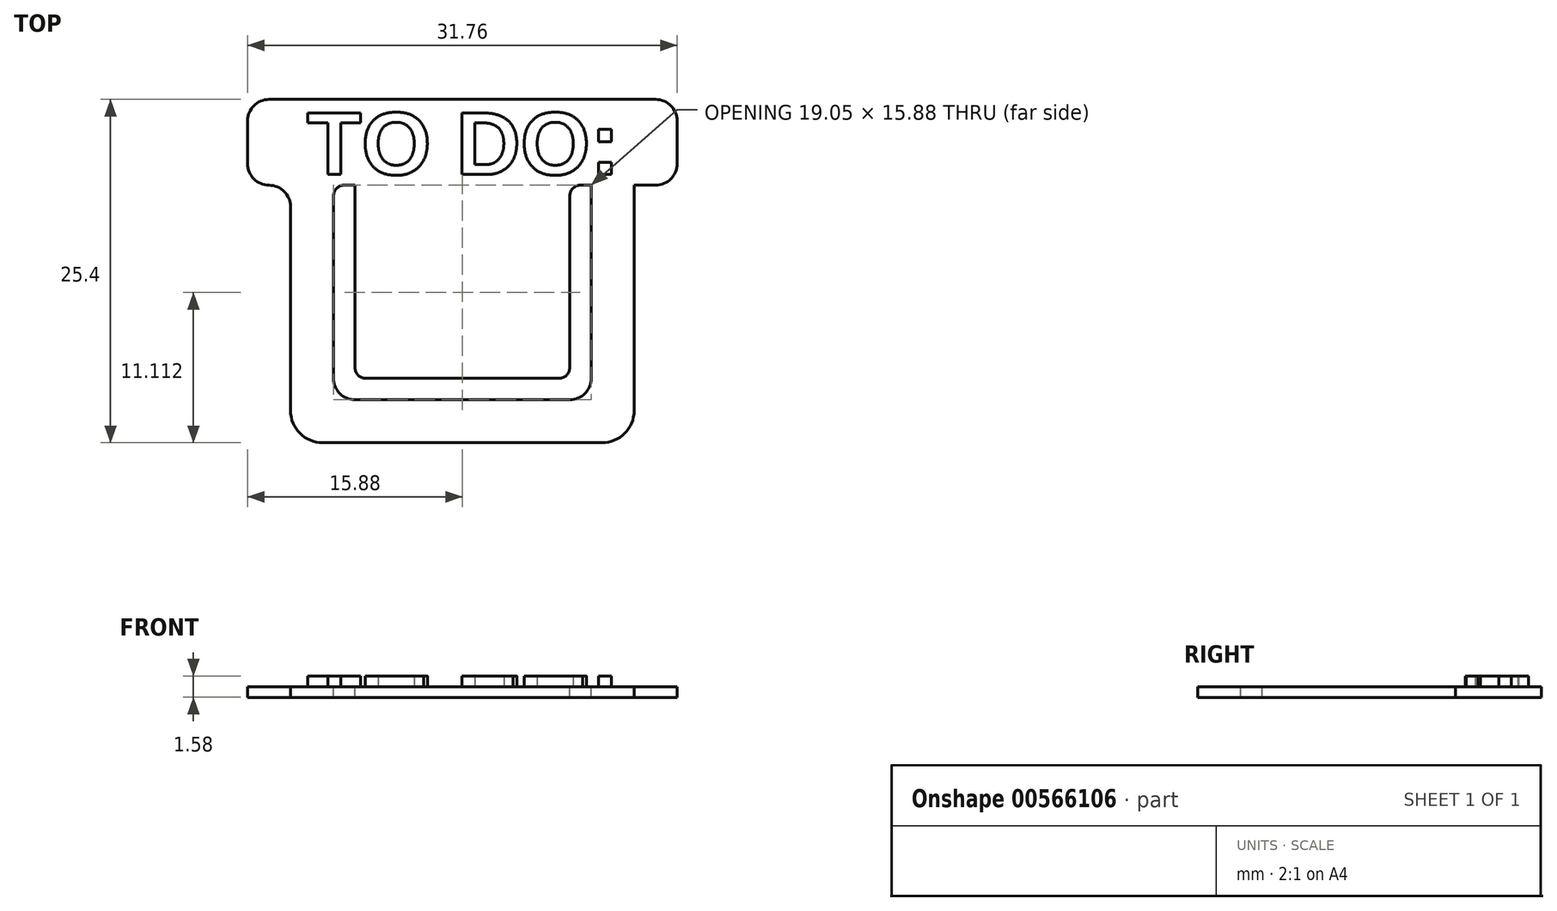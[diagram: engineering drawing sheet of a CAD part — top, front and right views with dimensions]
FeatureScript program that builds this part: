
annotation { "Feature Type Name" : "Feature", "Feature Type Description" : "" }
export const myFeature = defineFeature(function(context is Context, id is Id, definition is map)
    precondition{}
    {
        {
            var Q0;
            Q0=qCreatedBy(makeId("Front.planeOp"),FACE);
            var sketch = newSketch(context, id + "F0", { "sketchPlane" : qUnion([Q0])});
            skLineSegment(sketch, "E0.bottom", {"start": v(12.7, 9.53) * mm, "end": v(-12.7, 9.53) * mm});
            skLineSegment(sketch, "E0.top", {"start": v(12.7, -9.53) * mm, "end": v(-12.7, -9.53) * mm});
            skLineSegment(sketch, "E0.left", {"start": v(12.7, 9.53) * mm, "end": v(12.7, -9.53) * mm});
            skLineSegment(sketch, "E0.right", {"start": v(-12.7, 9.53) * mm, "end": v(-12.7, -9.53) * mm});
            skPoint(sketch, "E0.middle", {"position": v(0, 0) * mm});
            skSolve(sketch);
        }
        {
            var Q0;
            Q0=makeQuery(id+"F0.imprint","IMPRINT",FACE,{"disambiguationData":[TD([[makeQuery(id+"F0.imprint","IMPRINT",EDGE,{"derivedFrom":sQuery(id+"F0.wireOp",EDGE,"E0.bottom")}),1.0]])]});
            extrude(context, id + "F1", {"entities" : qUnion([Q0]), "depth" : 0.8 * mm, "offsetDistance" : 25.4 * mm});
        }
        {
            var Q0;
            Q0=makeQuery(id+"F1.opExtrude","SWEPT_EDGE",EDGE,{"disambiguationData":[OSD([sQuery(id+"F0.wireOp",EDGE,"E0.top"),sQuery(id+"F0.wireOp",EDGE,"E0.left")])]});
            var Q1;
            Q1=makeQuery(id+"F1.opExtrude","SWEPT_EDGE",EDGE,{"disambiguationData":[OSD([sQuery(id+"F0.wireOp",EDGE,"E0.top"),sQuery(id+"F0.wireOp",EDGE,"E0.right")])]});
            fillet(context, id + "F2", {"entities" : qUnion([Q0, Q1]), "radius" : 2.38 * mm, "tangentPropagation" : true, "allowEdgeOverflow" : false});
        }
        {
            var Q0;
            Q0=makeQuery(id+"F1.opExtrude","CAP_FACE",FACE,{"disambiguationData":[OSD([sQuery(id+"F0.wireOp",EDGE,"E0.bottom"),sQuery(id+"F0.wireOp",EDGE,"E0.top"),sQuery(id+"F0.wireOp",EDGE,"E0.left"),sQuery(id+"F0.wireOp",EDGE,"E0.right")])],"isStart":false});
            var sketch = newSketch(context, id + "F3", { "sketchPlane" : qUnion([Q0])});
            skLineSegment(sketch, "E1.bottom", {"start": v(9.52, 9.53) * mm, "end": v(-9.53, 9.53) * mm});
            skLineSegment(sketch, "E1.top", {"start": v(9.53, -6.35) * mm, "end": v(-9.53, -6.35) * mm});
            skLineSegment(sketch, "E1.left", {"start": v(9.52, 9.53) * mm, "end": v(9.53, -6.35) * mm});
            skLineSegment(sketch, "E1.right", {"start": v(-9.53, 9.53) * mm, "end": v(-9.52, -6.35) * mm});
            skPoint(sketch, "E1.middle", {"position": v(0, 0) * mm});
            skSolve(sketch);
        }
        {
            var Q0;
            Q0=makeQuery(id+"F3.imprint","IMPRINT",FACE,{"disambiguationData":[TD([[makeQuery(id+"F3.imprint","IMPRINT",EDGE,{"derivedFrom":sQuery(id+"F3.wireOp",EDGE,"E1.bottom")}),1.0]])]});
            extrude(context, id + "F4", {"entities" : qUnion([Q0]), "operationType" : NewBodyOperationType.REMOVE, "oppositeDirection" : true, "depth" : 4.93 * mm, "offsetDistance" : 25.4 * mm});
        }
        {
            var Q0;
            Q0=makeQuery(id+"F1.opExtrude","CAP_FACE",FACE,{"disambiguationData":[OSD([sQuery(id+"F0.wireOp",EDGE,"E0.bottom"),sQuery(id+"F0.wireOp",EDGE,"E0.top"),sQuery(id+"F0.wireOp",EDGE,"E0.left"),sQuery(id+"F0.wireOp",EDGE,"E0.right")])],"isStart":false});
            var sketch = newSketch(context, id + "F5", { "sketchPlane" : qUnion([Q0])});
            skLineSegment(sketch, "E2.bottom", {"start": v(-15.88, 9.53) * mm, "end": v(15.87, 9.53) * mm});
            skLineSegment(sketch, "E2.top", {"start": v(-15.88, 15.88) * mm, "end": v(15.87, 15.88) * mm});
            skLineSegment(sketch, "E2.left", {"start": v(-15.88, 9.53) * mm, "end": v(-15.88, 15.88) * mm});
            skLineSegment(sketch, "E2.right", {"start": v(15.87, 9.53) * mm, "end": v(15.87, 15.88) * mm});
            skSolve(sketch);
        }
        {
            var Q0;
            Q0=makeQuery(id+"F5.imprint","IMPRINT",FACE,{"disambiguationData":[TD([[makeQuery(id+"F5.imprint","IMPRINT",EDGE,{"derivedFrom":sQuery(id+"F5.wireOp",EDGE,"E2.top")}),-1.0]])]});
            extrude(context, id + "F6", {"entities" : qUnion([Q0]), "operationType" : NewBodyOperationType.ADD, "oppositeDirection" : true, "depth" : 0.8 * mm, "offsetDistance" : 25.4 * mm});
        }
        {
            var Q0;
            Q0=makeQuery(id+"F6.opExtrude","SWEPT_EDGE",EDGE,{"disambiguationData":[OSD([sQuery(id+"F5.wireOp",EDGE,"E2.top"),sQuery(id+"F5.wireOp",EDGE,"E2.left")])]});
            var Q1;
            Q1=makeQuery(id+"F6.opExtrude","SWEPT_EDGE",EDGE,{"disambiguationData":[OSD([sQuery(id+"F5.wireOp",EDGE,"E2.top"),sQuery(id+"F5.wireOp",EDGE,"E2.right")])]});
            var Q2;
            Q2=makeQuery(id+"F6.opExtrude","SWEPT_EDGE",EDGE,{"disambiguationData":[OSD([sQuery(id+"F5.wireOp",EDGE,"E2.bottom"),sQuery(id+"F5.wireOp",EDGE,"E2.right")])]});
            var Q3;
            Q3=makeQuery(id+"F1.opExtrude","SWEPT_EDGE",EDGE,{"disambiguationData":[OSD([sQuery(id+"F0.wireOp",EDGE,"E0.bottom"),sQuery(id+"F0.wireOp",EDGE,"E0.left")])]});
            var Q4;
            Q4=makeQuery(id+"F6.opExtrude","SWEPT_EDGE",EDGE,{"disambiguationData":[OSD([sQuery(id+"F5.wireOp",EDGE,"E2.bottom"),sQuery(id+"F5.wireOp",EDGE,"E2.left")])]});
            var Q5;
            Q5=makeQuery(id+"F1.opExtrude","SWEPT_EDGE",EDGE,{"disambiguationData":[OSD([sQuery(id+"F0.wireOp",EDGE,"E0.bottom"),sQuery(id+"F0.wireOp",EDGE,"E0.right")])]});
            fillet(context, id + "F7", {"entities" : qUnion([Q0, Q1, Q2, Q3, Q4, Q5]), "radius" : 1.59 * mm, "tangentPropagation" : true, "allowEdgeOverflow" : false});
        }
        {
            var Q0;
            Q0=makeQuery(id+"F4.boolean.opBoolean","COPY",EDGE,{"derivedFrom":makeQuery(id+"F4.opExtrude","SWEPT_EDGE",EDGE,{"disambiguationData":[OSD([sQuery(id+"F3.wireOp",EDGE,"E1.top"),sQuery(id+"F3.wireOp",EDGE,"E1.right")])]})});
            var Q1;
            Q1=makeQuery(id+"F4.boolean.opBoolean","COPY",EDGE,{"derivedFrom":makeQuery(id+"F4.opExtrude","SWEPT_EDGE",EDGE,{"disambiguationData":[OSD([sQuery(id+"F3.wireOp",EDGE,"E1.top"),sQuery(id+"F3.wireOp",EDGE,"E1.left")])]})});
            fillet(context, id + "F8", {"entities" : qUnion([Q0, Q1]), "radius" : 1.59 * mm, "tangentPropagation" : true, "allowEdgeOverflow" : false});
        }
        {
            var Q0;
            Q0=makeQuery(id+"F6.boolean.opBoolean","MERGE",FACE,{"derivedFrom":[makeQuery(id+"F1.opExtrude","CAP_FACE",FACE,{"disambiguationData":[OSD([sQuery(id+"F0.wireOp",EDGE,"E0.bottom"),sQuery(id+"F0.wireOp",EDGE,"E0.top"),sQuery(id+"F0.wireOp",EDGE,"E0.left"),sQuery(id+"F0.wireOp",EDGE,"E0.right")])],"isStart":false}),makeQuery(id+"F6.opExtrude","CAP_FACE",FACE,{"disambiguationData":[OSD([sQuery(id+"F5.wireOp",EDGE,"E2.bottom"),sQuery(id+"F5.wireOp",EDGE,"E2.top"),sQuery(id+"F5.wireOp",EDGE,"E2.left"),sQuery(id+"F5.wireOp",EDGE,"E2.right")])],"isStart":true})]});
            var sketch = newSketch(context, id + "F9", { "sketchPlane" : qUnion([Q0])});
            skLineSegment(sketch, "E3.bottom", {"start": v(-7.94, 9.53) * mm, "end": v(7.94, 9.53) * mm});
            skLineSegment(sketch, "E3.top", {"start": v(-7.94, -4.76) * mm, "end": v(7.94, -4.76) * mm});
            skLineSegment(sketch, "E3.left", {"start": v(-7.94, 9.53) * mm, "end": v(-7.94, -4.76) * mm});
            skLineSegment(sketch, "E3.right", {"start": v(7.94, 9.53) * mm, "end": v(7.94, -4.76) * mm});
            skSolve(sketch);
        }
        {
            var Q0;
            Q0=makeQuery(id+"F9.imprint","IMPRINT",FACE,{"disambiguationData":[TD([[makeQuery(id+"F9.imprint","IMPRINT",EDGE,{"derivedFrom":sQuery(id+"F9.wireOp",EDGE,"E3.bottom")}),1.0]])]});
            extrude(context, id + "F10", {"entities" : qUnion([Q0]), "operationType" : NewBodyOperationType.ADD, "oppositeDirection" : true, "depth" : 0.8 * mm, "offsetDistance" : 25.4 * mm});
        }
        {
            var Q0;
            Q0=makeQuery(id+"F10.boolean.opBoolean","MERGE",FACE,{"derivedFrom":[makeQuery(id+"F6.boolean.opBoolean","MERGE",FACE,{"derivedFrom":[makeQuery(id+"F1.opExtrude","CAP_FACE",FACE,{"disambiguationData":[OSD([sQuery(id+"F0.wireOp",EDGE,"E0.bottom"),sQuery(id+"F0.wireOp",EDGE,"E0.top"),sQuery(id+"F0.wireOp",EDGE,"E0.left"),sQuery(id+"F0.wireOp",EDGE,"E0.right")])],"isStart":false}),makeQuery(id+"F6.opExtrude","CAP_FACE",FACE,{"disambiguationData":[OSD([sQuery(id+"F5.wireOp",EDGE,"E2.bottom"),sQuery(id+"F5.wireOp",EDGE,"E2.top"),sQuery(id+"F5.wireOp",EDGE,"E2.left"),sQuery(id+"F5.wireOp",EDGE,"E2.right")])],"isStart":true})]}),makeQuery(id+"F10.opExtrude","CAP_FACE",FACE,{"disambiguationData":[OSD([sQuery(id+"F9.wireOp",EDGE,"E3.bottom"),sQuery(id+"F9.wireOp",EDGE,"E3.top"),sQuery(id+"F9.wireOp",EDGE,"E3.left"),sQuery(id+"F9.wireOp",EDGE,"E3.right")])],"isStart":true})]});
            var sketch = newSketch(context, id + "F11", { "sketchPlane" : qUnion([Q0])});
            skText(sketch, "E4", { "text": "TO DO:", "fontName": "Arimo-Bold.ttf"});
            const initialGuessF11  = {"E4": [-0.01149, 0.01032, 1, 0, 0.00476]};
            skSetInitialGuess(sketch, initialGuessF11);
            skSolve(sketch);
        }
        {
            var Q0;
            Q0=makeQuery(id+"F11.imprint","IMPRINT",FACE,{"disambiguationData":[TD([[makeQuery(id+"F11.imprint","IMPRINT",EDGE,{"derivedFrom":sQuery(id+"F11.wireOp",EDGE,"E4.sketch_text.stroke-0")}),-1.0]])]});
            var Q1;
            Q1=makeQuery(id+"F11.imprint","IMPRINT",FACE,{"disambiguationData":[TD([[makeQuery(id+"F11.imprint","IMPRINT",EDGE,{"derivedFrom":sQuery(id+"F11.wireOp",EDGE,"E4.sketch_text.stroke-8")}),-1.0]])]});
            var Q2;
            Q2=makeQuery(id+"F11.imprint","IMPRINT",FACE,{"disambiguationData":[TD([[makeQuery(id+"F11.imprint","IMPRINT",EDGE,{"derivedFrom":sQuery(id+"F11.wireOp",EDGE,"E4.sketch_text.stroke-25")}),-1.0]])]});
            var Q3;
            Q3=makeQuery(id+"F11.imprint","IMPRINT",FACE,{"disambiguationData":[TD([[makeQuery(id+"F11.imprint","IMPRINT",EDGE,{"derivedFrom":sQuery(id+"F11.wireOp",EDGE,"E4.sketch_text.stroke-40")}),-1.0]])]});
            var Q4;
            Q4=makeQuery(id+"F11.imprint","IMPRINT",FACE,{"disambiguationData":[TD([[makeQuery(id+"F11.imprint","IMPRINT",EDGE,{"derivedFrom":sQuery(id+"F11.wireOp",EDGE,"E4.sketch_text.stroke-55")}),-1.0]])]});
            var Q5;
            Q5=makeQuery(id+"F11.imprint","IMPRINT",FACE,{"disambiguationData":[TD([[makeQuery(id+"F11.imprint","IMPRINT",EDGE,{"derivedFrom":sQuery(id+"F11.wireOp",EDGE,"E4.sketch_text.stroke-57")}),-1.0]])]});
            var Q6;
            Q6=makeQuery(id+"F11.imprint","IMPRINT",FACE,{"disambiguationData":[TD([[makeQuery(id+"F11.imprint","IMPRINT",EDGE,{"derivedFrom":sQuery(id+"F11.wireOp",EDGE,"E4.sketch_text.stroke-61")}),-1.0]])]});
            extrude(context, id + "F12", {"entities" : qUnion([Q0, Q1, Q2, Q3, Q4, Q5, Q6]), "operationType" : NewBodyOperationType.ADD, "depth" : 0.8 * mm, "offsetDistance" : 25.4 * mm});
        }
        {
            var Q0;
            Q0=makeQuery(id+"F10.opExtrude","SWEPT_EDGE",EDGE,{"disambiguationData":[OSD([sQuery(id+"F5.wireOp",EDGE,"E2.bottom"),sQuery(id+"F9.wireOp",EDGE,"E3.bottom"),sQuery(id+"F9.wireOp",EDGE,"E3.left")])]});
            var Q1;
            Q1=makeQuery(id+"F4.boolean.opBoolean","COPY",EDGE,{"derivedFrom":makeQuery(id+"F4.opExtrude","SWEPT_EDGE",EDGE,{"disambiguationData":[OSD([sQuery(id+"F0.wireOp",EDGE,"E0.bottom"),sQuery(id+"F3.wireOp",EDGE,"E1.bottom"),sQuery(id+"F3.wireOp",EDGE,"E1.right")])]})});
            var Q2;
            Q2=makeQuery(id+"F10.opExtrude","SWEPT_EDGE",EDGE,{"disambiguationData":[OSD([sQuery(id+"F5.wireOp",EDGE,"E2.bottom"),sQuery(id+"F9.wireOp",EDGE,"E3.bottom"),sQuery(id+"F9.wireOp",EDGE,"E3.right")])]});
            var Q3;
            Q3=makeQuery(id+"F4.boolean.opBoolean","COPY",EDGE,{"derivedFrom":makeQuery(id+"F4.opExtrude","SWEPT_EDGE",EDGE,{"disambiguationData":[OSD([sQuery(id+"F0.wireOp",EDGE,"E0.bottom"),sQuery(id+"F3.wireOp",EDGE,"E1.bottom"),sQuery(id+"F3.wireOp",EDGE,"E1.left")])]})});
            fillet(context, id + "F13", {"entities" : qUnion([Q0, Q1, Q2, Q3]), "radius" : 0.8 * mm, "tangentPropagation" : true, "allowEdgeOverflow" : false});
        }
        {
            var Q0;
            Q0=makeQuery(id+"F10.opExtrude","SWEPT_EDGE",EDGE,{"disambiguationData":[OSD([sQuery(id+"F9.wireOp",EDGE,"E3.top"),sQuery(id+"F9.wireOp",EDGE,"E3.left")])]});
            var Q1;
            Q1=makeQuery(id+"F10.opExtrude","SWEPT_EDGE",EDGE,{"disambiguationData":[OSD([sQuery(id+"F9.wireOp",EDGE,"E3.top"),sQuery(id+"F9.wireOp",EDGE,"E3.right")])]});
            fillet(context, id + "F14", {"entities" : qUnion([Q0, Q1]), "radius" : 0.8 * mm, "tangentPropagation" : true, "allowEdgeOverflow" : false});
        }
        {
            var Q0;
            Q0=makeQuery(id+"F1.opExtrude","SWEPT_BODY",BODY,{"disambiguationData":[OSD([sQuery(id+"F0.wireOp",EDGE,"E0.bottom"),sQuery(id+"F0.wireOp",EDGE,"E0.top"),sQuery(id+"F0.wireOp",EDGE,"E0.left"),sQuery(id+"F0.wireOp",EDGE,"E0.right")])]});
            var Q1;
            Q1=makeQuery(id+"F6.opExtrude","CAP_EDGE",EDGE,{"disambiguationData":[OSD([sQuery(id+"F5.wireOp",EDGE,"E2.top")])],"isStart":false});
            transform(context, id + "F15", {"entities" : qUnion([Q0]), "transformType" : TransformType.ROTATION, "transformAxis" : qUnion([Q1]), "angle" : 270 * degree, "makeCopy" : false});
        }
    });
